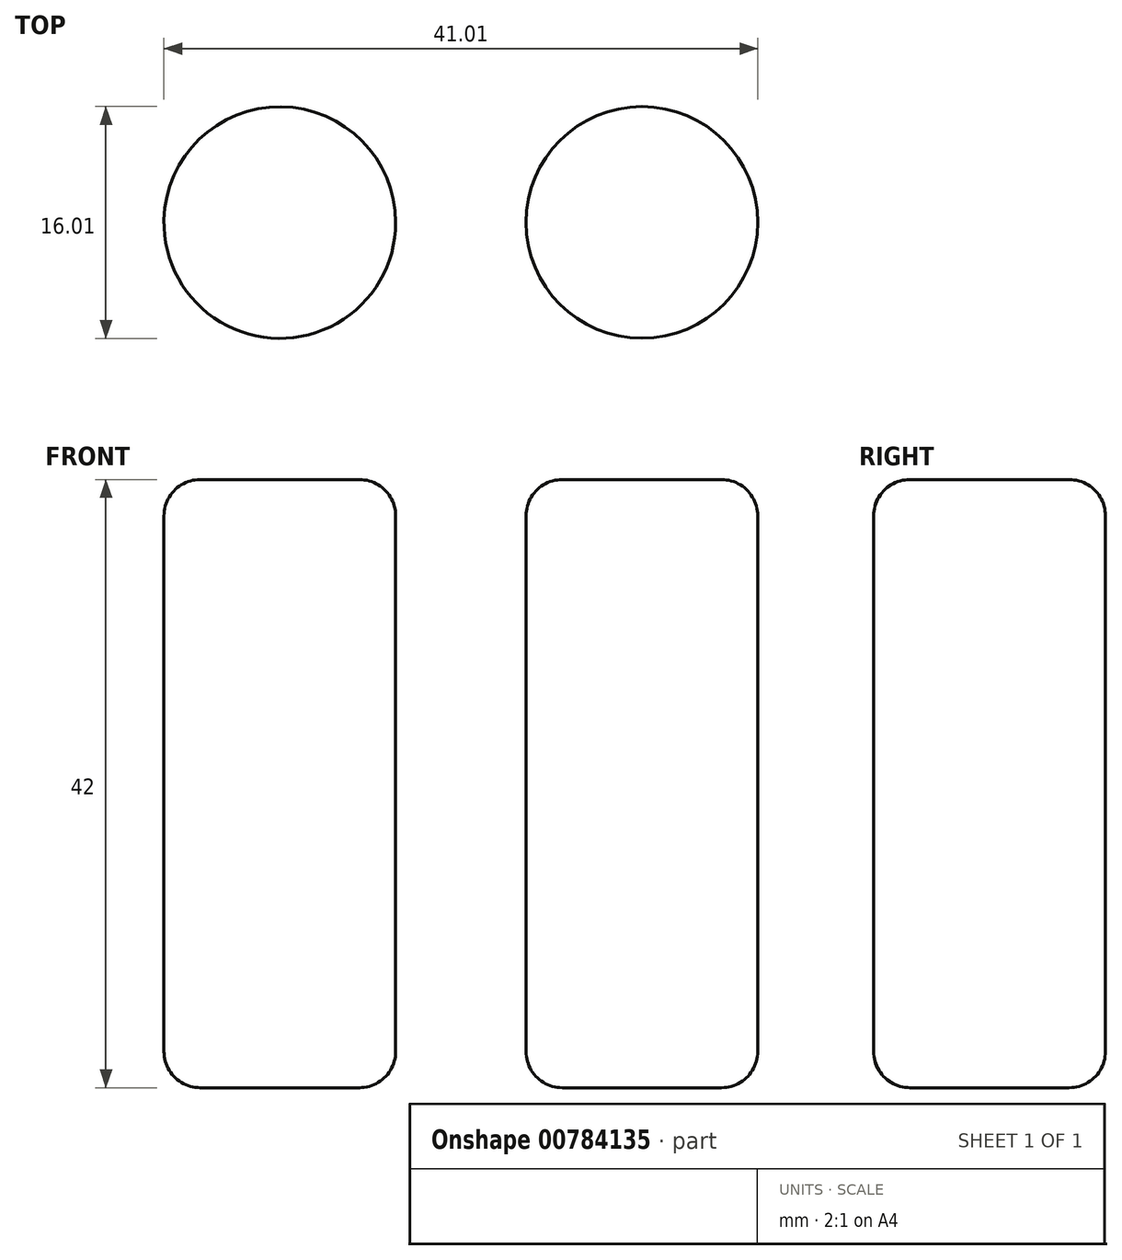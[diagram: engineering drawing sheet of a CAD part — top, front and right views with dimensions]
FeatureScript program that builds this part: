
annotation { "Feature Type Name" : "Feature", "Feature Type Description" : "" }
export const myFeature = defineFeature(function(context is Context, id is Id, definition is map)
    precondition{}
    {
        {
            var Q0;
            Q0=qCreatedBy(makeId("Top.planeOp"),FACE);
            var sketch = newSketch(context, id + "F0", { "sketchPlane" : qUnion([Q0])});
            skArc(sketch, "E0", {"start": v(-29.38, 37.31) * mm, "mid": v(-37.3, 45.3) * mm, "end": v(-45.38, 37.5) * mm});
            skArc(sketch, "E1", {"start": v(-45.38, 37.5) * mm, "mid": v(-37.47, 29.3) * mm, "end": v(-29.38, 37.31) * mm});
            skArc(sketch, "E2.1.0.0", {"start": v(-20.37, 37.4) * mm, "mid": v(-12.47, 29.31) * mm, "end": v(-4.37, 37.22) * mm});
            skArc(sketch, "E3.1.0.0", {"start": v(-4.37, 37.22) * mm, "mid": v(-12.28, 45.3) * mm, "end": v(-20.37, 37.4) * mm});
            skPoint(sketch, "E4.startSnap0", {"position": v(-37.3, 45.3) * mm});
            skSolve(sketch);
        }
        {
            var Q0;
            Q0 = qSketchRegion(id + "F0", true);
            extrude(context, id + "F1", {"entities" : qUnion([Q0]), "depth" : 42 * mm, "offsetDistance" : 25 * mm});
        }
        {
            var Q0;
            Q0=makeQuery(id+"F1.opExtrude","CAP_FACE",FACE,{"disambiguationData":[OSD([sQuery(id+"F0.wireOp",EDGE,"E2.1.0.0"),sQuery(id+"F0.wireOp",EDGE,"E3.1.0.0")])],"isStart":false});
            var Q1;
            Q1=makeQuery(id+"F1.opExtrude","CAP_FACE",FACE,{"disambiguationData":[OSD([sQuery(id+"F0.wireOp",EDGE,"E0"),sQuery(id+"F0.wireOp",EDGE,"E1")])],"isStart":false});
            var Q2;
            Q2=makeQuery(id+"F1.opExtrude","CAP_FACE",FACE,{"disambiguationData":[OSD([sQuery(id+"F0.wireOp",EDGE,"E0"),sQuery(id+"F0.wireOp",EDGE,"E1")])],"isStart":true});
            var Q3;
            Q3=makeQuery(id+"F1.opExtrude","CAP_FACE",FACE,{"disambiguationData":[OSD([sQuery(id+"F0.wireOp",EDGE,"E2.1.0.0"),sQuery(id+"F0.wireOp",EDGE,"E3.1.0.0")])],"isStart":true});
            fillet(context, id + "F2", {"entities" : qUnion([Q0, Q1, Q2, Q3]), "radius" : 2.5 * mm, "tangentPropagation" : true, "allowEdgeOverflow" : false});
        }
    });
